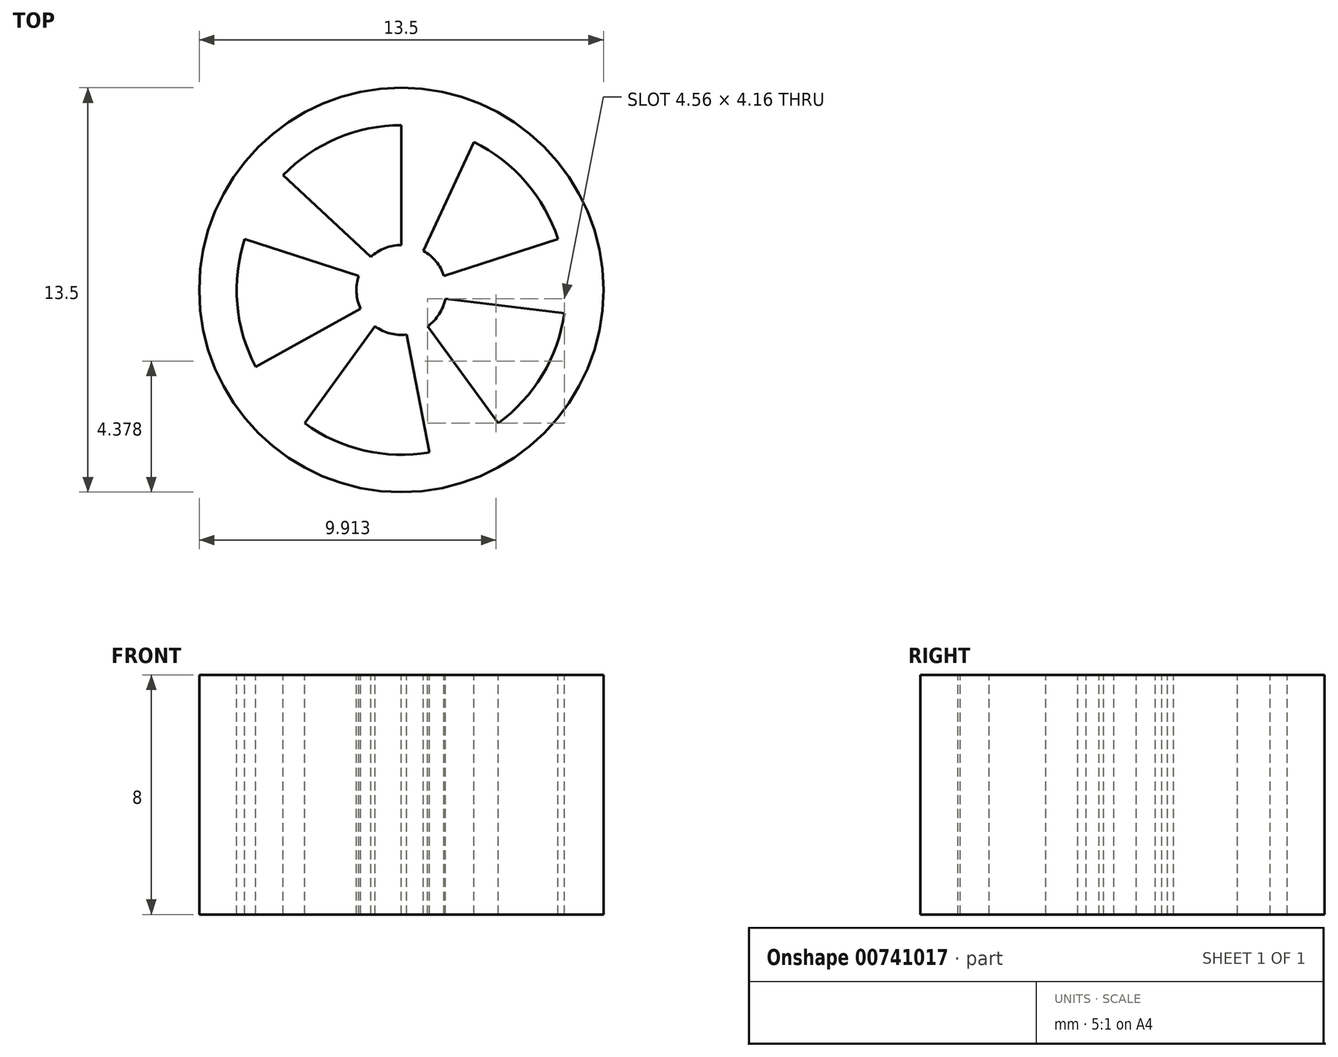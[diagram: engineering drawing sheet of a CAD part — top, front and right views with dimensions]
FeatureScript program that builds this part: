
annotation { "Feature Type Name" : "Feature", "Feature Type Description" : "" }
export const myFeature = defineFeature(function(context is Context, id is Id, definition is map)
    precondition{}
    {
        {
            var Q0;
            Q0=qCreatedBy(makeId("Top.planeOp"),FACE);
            var sketch = newSketch(context, id + "F0", { "sketchPlane" : qUnion([Q0])});
            skCircle(sketch, "E0", {"center": v(0, 0) * mm, "radius": 6.75 * mm});
            skSolve(sketch);
        }
        {
            var Q0;
            Q0=makeQuery(id+"F0.imprint","IMPRINT",FACE,{"disambiguationData":[TD([[makeQuery(id+"F0.imprint","IMPRINT",EDGE,{"derivedFrom":sQuery(id+"F0.wireOp",EDGE,"E0")}),1.0]])]});
            extrude(context, id + "F1", {"entities" : qUnion([Q0]), "depth" : 8 * mm, "offsetDistance" : 25 * mm});
        }
        {
            var Q0;
            Q0=makeQuery(id+"F1.opExtrude","CAP_FACE",FACE,{"disambiguationData":[OSD([sQuery(id+"F0.wireOp",EDGE,"E0")])],"isStart":false});
            var sketch = newSketch(context, id + "F2", { "sketchPlane" : qUnion([Q0])});
            skCircle(sketch, "E1", {"center": v(0, 0) * mm, "radius": 5.5 * mm});
            skCircle(sketch, "E2", {"center": v(0, 0) * mm, "radius": 1.5 * mm});
            skLineSegment(sketch, "E3", {"start": v(0, 1.5) * mm, "end": v(0, 5.5) * mm});
            skLineSegment(sketch, "E4", {"start": v(0.73, 1.3) * mm, "end": v(2.43, 4.94) * mm});
            skLineSegment(sketch, "E5.1.0", {"start": v(-1.43, 0.46) * mm, "end": v(-5.23, 1.7) * mm});
            skLineSegment(sketch, "E5.1.1", {"start": v(-1.02, 1.1) * mm, "end": v(-3.94, 3.83) * mm});
            skLineSegment(sketch, "E5.2.0", {"start": v(-0.88, -1.21) * mm, "end": v(-3.23, -4.45) * mm});
            skLineSegment(sketch, "E5.2.1", {"start": v(-1.36, -0.63) * mm, "end": v(-4.86, -2.57) * mm});
            skLineSegment(sketch, "E5.3.0", {"start": v(0.88, -1.21) * mm, "end": v(3.23, -4.45) * mm});
            skLineSegment(sketch, "E5.3.1", {"start": v(0.18, -1.49) * mm, "end": v(0.94, -5.42) * mm});
            skLineSegment(sketch, "E5.4.0", {"start": v(1.43, 0.46) * mm, "end": v(5.23, 1.7) * mm});
            skLineSegment(sketch, "E5.4.1", {"start": v(1.47, -0.3) * mm, "end": v(5.44, -0.78) * mm});
            skSolve(sketch);
        }
        {
            var Q0;
            {var subQ0=sQuery(id+"F2.wireOp",EDGE,"E3");Q0=makeQuery(id+"F2.imprint","IMPRINT",FACE,{"disambiguationData":[TD([[makeQuery(id+"F2.imprint","IMPRINT",EDGE,{"derivedFrom":subQ0}),1.0]])]});}
            var Q1;
            {var subQ0=sQuery(id+"F2.wireOp",EDGE,"E4");Q1=makeQuery(id+"F2.imprint","IMPRINT",FACE,{"disambiguationData":[TD([[makeQuery(id+"F2.imprint","IMPRINT",EDGE,{"derivedFrom":subQ0}),-1.0]])]});}
            var Q2;
            {var subQ0=sQuery(id+"F2.wireOp",EDGE,"E5.3.0");Q2=makeQuery(id+"F2.imprint","IMPRINT",FACE,{"disambiguationData":[TD([[makeQuery(id+"F2.imprint","IMPRINT",EDGE,{"derivedFrom":subQ0}),1.0]])]});}
            var Q3;
            {var subQ0=sQuery(id+"F2.wireOp",EDGE,"E5.2.0");Q3=makeQuery(id+"F2.imprint","IMPRINT",FACE,{"disambiguationData":[TD([[makeQuery(id+"F2.imprint","IMPRINT",EDGE,{"derivedFrom":subQ0}),1.0]])]});}
            var Q4;
            {var subQ0=sQuery(id+"F2.wireOp",EDGE,"E5.1.0");Q4=makeQuery(id+"F2.imprint","IMPRINT",FACE,{"disambiguationData":[TD([[makeQuery(id+"F2.imprint","IMPRINT",EDGE,{"derivedFrom":subQ0}),1.0]])]});}
            extrude(context, id + "F3", {"entities" : qUnion([Q0, Q1, Q2, Q3, Q4]), "operationType" : NewBodyOperationType.REMOVE, "endBound" : BoundingType.THROUGH_ALL, "oppositeDirection" : true, "depth" : 25 * mm, "offsetDistance" : 25 * mm});
        }
    });
